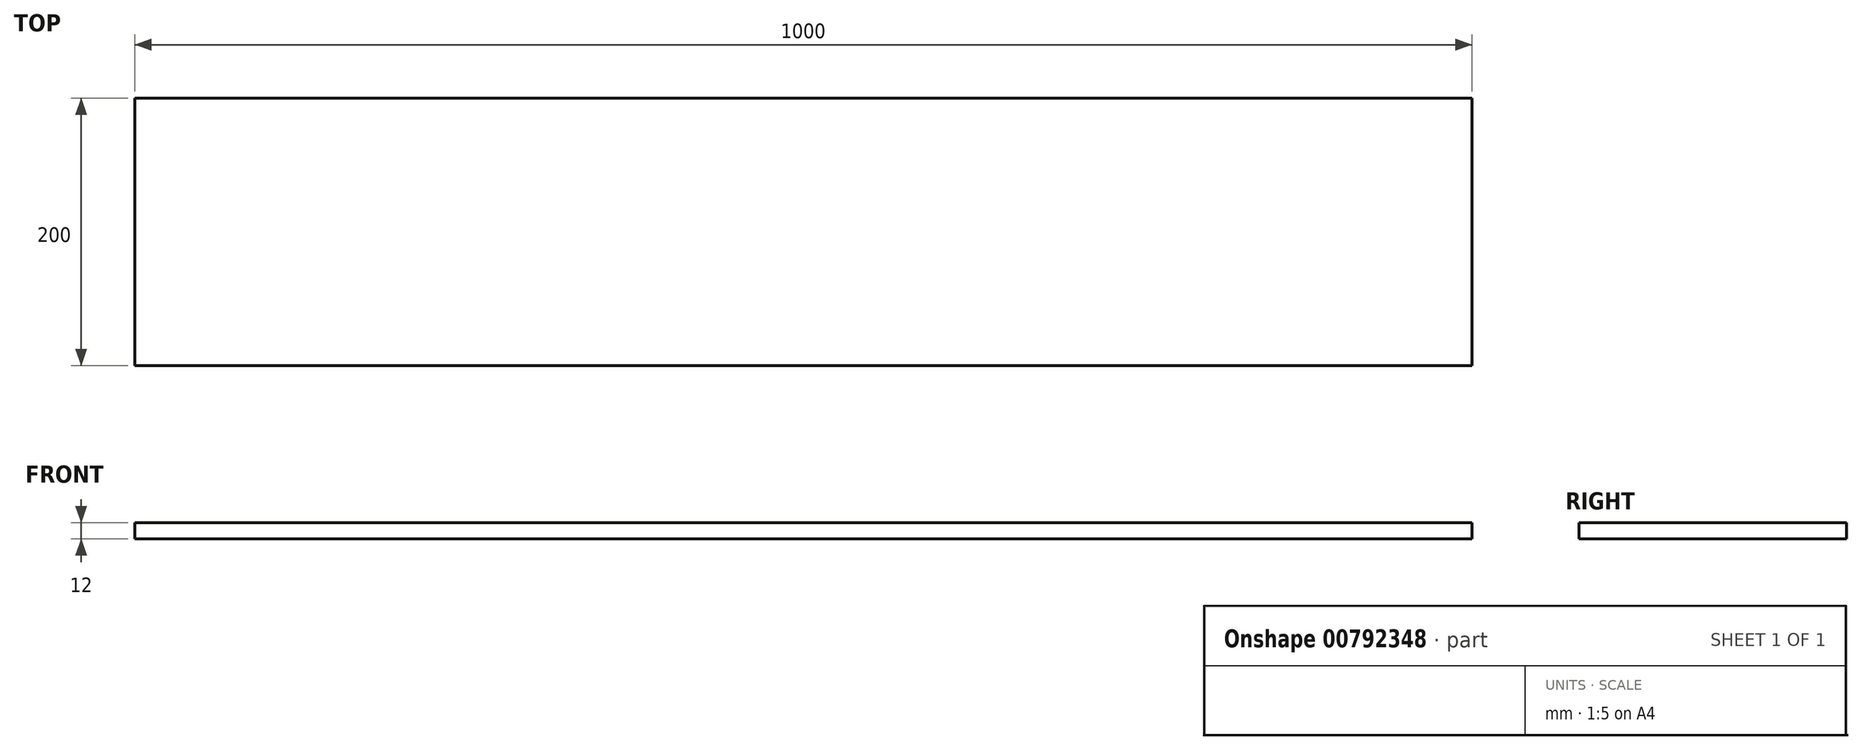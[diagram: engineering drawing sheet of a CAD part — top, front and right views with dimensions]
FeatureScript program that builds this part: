
annotation { "Feature Type Name" : "Feature", "Feature Type Description" : "" }
export const myFeature = defineFeature(function(context is Context, id is Id, definition is map)
    precondition{}
    {
        {
            var Q0;
            Q0=qCreatedBy(makeId("Top.planeOp"),FACE);
            var sketch = newSketch(context, id + "F0", { "sketchPlane" : qUnion([Q0])});
            skLineSegment(sketch, "E0.bottom", {"start": v(500, 100) * mm, "end": v(-500, 100) * mm});
            skLineSegment(sketch, "E0.top", {"start": v(500, -100) * mm, "end": v(-500, -100) * mm});
            skLineSegment(sketch, "E0.left", {"start": v(500, 100) * mm, "end": v(500, -100) * mm});
            skLineSegment(sketch, "E0.right", {"start": v(-500, 100) * mm, "end": v(-500, -100) * mm});
            skPoint(sketch, "E0.middle", {"position": v(0, 0) * mm});
            skLineSegment(sketch, "E1", {"start": v(0, -100) * mm, "end": v(0, 100) * mm, "construction": true});
            skSolve(sketch);
        }
        {
            var Q0;
            Q0 = qSketchRegion(id + "F0", true);
            extrude(context, id + "F1", {"entities" : qUnion([Q0]), "depth" : 12 * mm, "offsetDistance" : 25 * mm});
        }
    });
